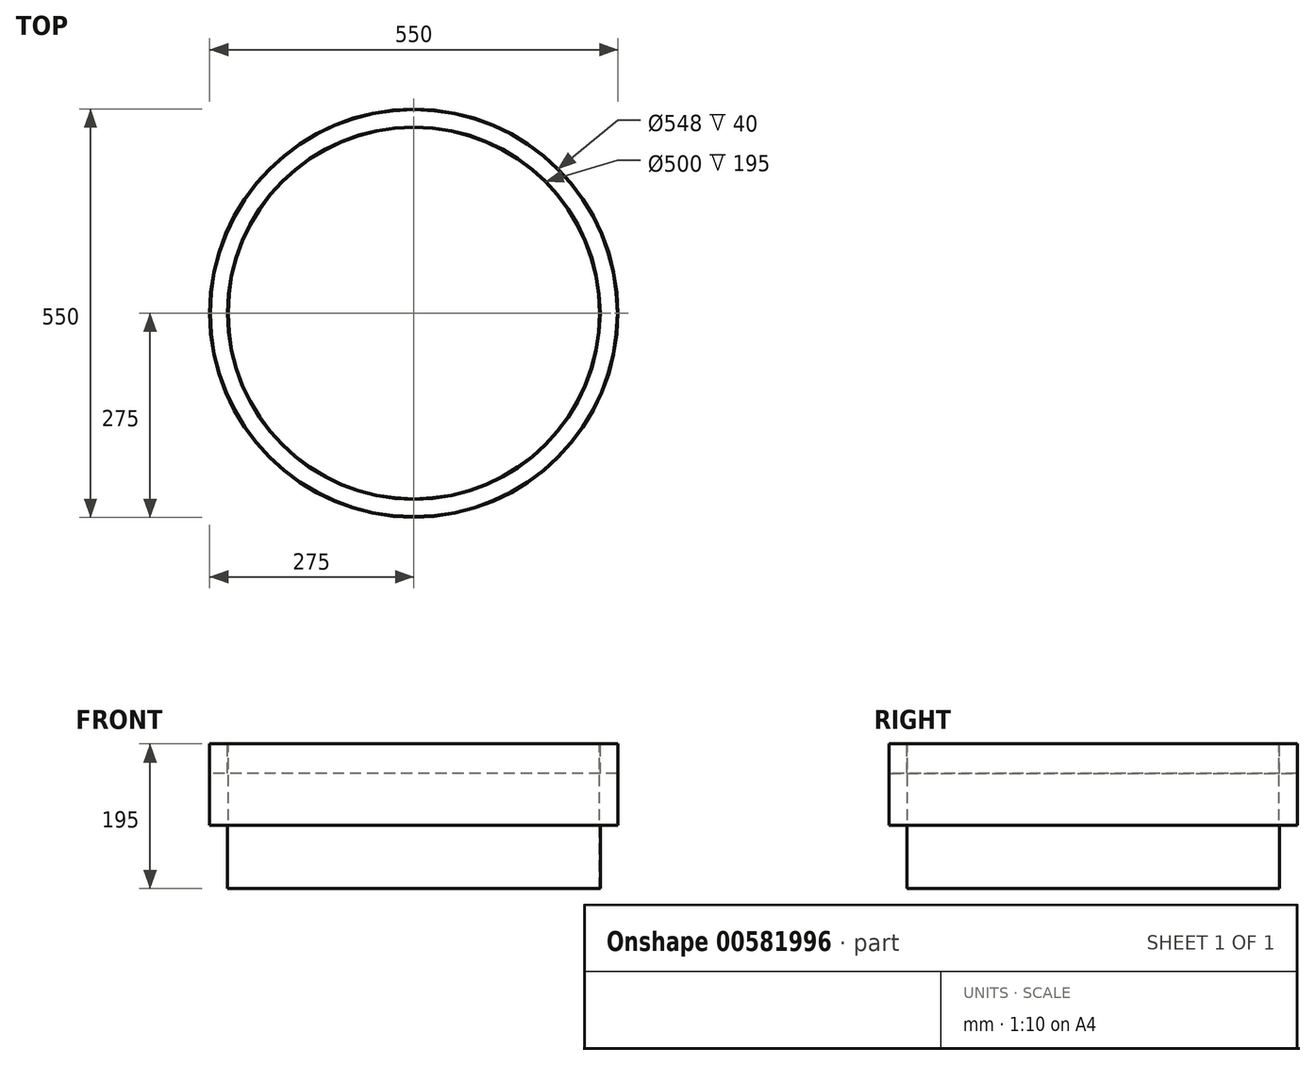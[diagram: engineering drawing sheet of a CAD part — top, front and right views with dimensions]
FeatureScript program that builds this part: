
annotation { "Feature Type Name" : "Feature", "Feature Type Description" : "" }
export const myFeature = defineFeature(function(context is Context, id is Id, definition is map)
    precondition{}
    {
        {
            var Q0;
            Q0=qCreatedBy(makeId("Front.planeOp"),FACE);
            var sketch = newSketch(context, id + "F0", { "sketchPlane" : qUnion([Q0])});
            skLineSegment(sketch, "E0", {"start": v(0, 710.75) * mm, "end": v(0, -704.58) * mm, "construction": true});
            skLineSegment(sketch, "E1", {"start": v(-250, 215.65) * mm, "end": v(-250, 410.65) * mm});
            skLineSegment(sketch, "E2", {"start": v(-250, 410.65) * mm, "end": v(-251, 410.65) * mm});
            skLineSegment(sketch, "E3", {"start": v(-274, 410.65) * mm, "end": v(-275, 410.65) * mm});
            skLineSegment(sketch, "E4", {"start": v(-275, 410.65) * mm, "end": v(-275, 300.65) * mm});
            skLineSegment(sketch, "E5", {"start": v(-275, 300.65) * mm, "end": v(-251, 300.65) * mm});
            skLineSegment(sketch, "E6", {"start": v(-251, 300.65) * mm, "end": v(-251, 215.65) * mm});
            skLineSegment(sketch, "E7", {"start": v(-274, 410.65) * mm, "end": v(-274, 370.65) * mm});
            skLineSegment(sketch, "E8", {"start": v(-274, 370.65) * mm, "end": v(-251, 370.65) * mm});
            skLineSegment(sketch, "E9", {"start": v(-251, 370.65) * mm, "end": v(-251, 410.65) * mm});
            skLineSegment(sketch, "E10", {"start": v(-251, 215.65) * mm, "end": v(-250, 215.65) * mm});
            skSolve(sketch);
        }
        {
            var Q0;
            Q0=qSketchRegion(id+"F0",true);
            var Q1;
            Q1=sQuery(id+"F0.wireOp",EDGE,"E0");
            revolve(context, id + "F1", {"entities" : qUnion([Q0]), "axis" : qUnion([Q1]), "revolveType" : RevolveType.FULL});
        }
    });
